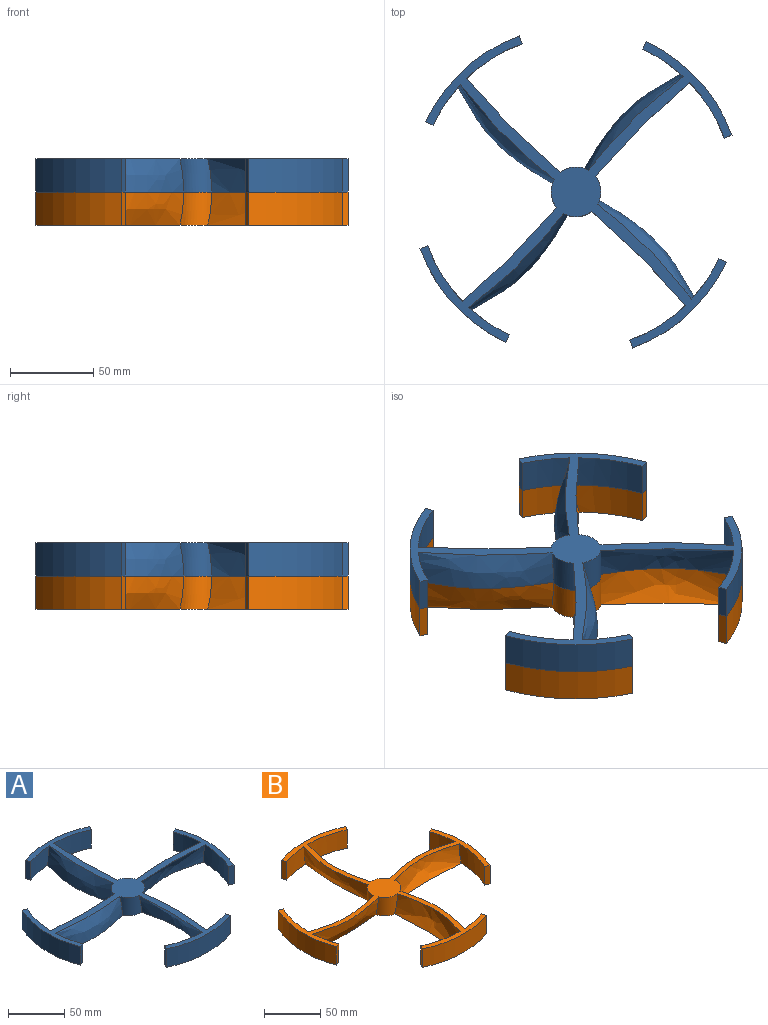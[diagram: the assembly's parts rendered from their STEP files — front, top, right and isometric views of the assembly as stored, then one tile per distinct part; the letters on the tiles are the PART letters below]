
ASSEMBLY  parts=2 mates=1
PART A: 34 faces, bbox 200.4x200.4x20.4 mm
  f0: cylinder r=15mm len=20mm, axis (0,0,-1), area 366.7mm2, adj f3,f4,f6,f14
  f1: cylinder r=15mm len=20mm, axis (0,0,-1), area 366.7mm2, adj f3,f4,f7,f21
  f2: cylinder r=15mm len=20mm, axis (0,0,-1), area 366.7mm2, adj f3,f4,f13,f23
  f3: plane 200.42x200.42mm, normal (0,0,1), area 4211.3mm2, adj f0,f1,f2,f5,f6,f7,f8,f9
  f4: plane 200.29x200.29mm, normal (0,0,-1), area 3850.5mm2, adj f0,f1,f2,f5,f6,f7,f8,f9
  f5: cylinder r=15mm len=20mm, axis (0,0,-1), area 366.7mm2, adj f3,f4,f20,f22
  f6: bspline ~81.35x20mm, area 1709.6mm2, adj f0,f3,f4,f29
  f7: bspline ~80.1x20mm, area 1727.7mm2, adj f1,f3,f4,f30
  f8: cylinder r=95mm len=28.78mm, axis (0,0,-1), area 568.9mm2, adj f3,f4,f9,f13
  f9: plane 20x4.7mm, normal (-0.34,0.94,0), area 100mm2, adj f3,f4,f8,f10
  f10: cylinder r=100mm len=76.46mm, axis (0,0,-1), area 1570.8mm2, adj f3,f4,f9,f11
  f11: plane 20x4.53mm, normal (-0.42,-0.91,0), area 100mm2, adj f3,f4,f10,f12
  f12: cylinder r=95mm len=40.82mm, axis (0,0,-1), area 818.3mm2, adj f3,f4,f11,f14
  f13: bspline ~81.35x20mm, area 1709.6mm2, adj f2,f3,f4,f8
  f14: bspline ~80.1x20mm, area 1727.7mm2, adj f0,f3,f4,f12
  f15: cylinder r=95mm len=28.78mm, axis (0,0,-1), area 568.9mm2, adj f3,f4,f16,f21
  f16: plane 20x4.7mm, normal (0.34,-0.94,0), area 100mm2, adj f3,f4,f15,f17
  f17: cylinder r=100mm len=76.46mm, axis (0,0,-1), area 1570.8mm2, adj f3,f4,f16,f18
  f18: plane 20x4.53mm, normal (0.42,0.91,0), area 100mm2, adj f3,f4,f17,f19
  f19: cylinder r=95mm len=40.82mm, axis (0,0,-1), area 818.3mm2, adj f3,f4,f18,f20
  f20: bspline ~80.1x20mm, area 1727.7mm2, adj f3,f4,f5,f19
  f21: bspline ~81.35x20mm, area 1709.6mm2, adj f1,f3,f4,f15
  f22: bspline ~81.35x20mm, area 1709.6mm2, adj f3,f4,f5,f24
  f23: bspline ~80.1x20mm, area 1727.7mm2, adj f2,f3,f4,f28
  f24: cylinder r=95mm len=28.78mm, axis (0,0,-1), area 568.9mm2, adj f3,f4,f22,f27
  f25: plane 20x4.53mm, normal (0.91,-0.42,0), area 100mm2, adj f3,f4,f26,f28
  f26: cylinder r=100mm len=76.46mm, axis (0,0,-1), area 1570.8mm2, adj f3,f4,f25,f27
  f27: plane 20x4.7mm, normal (-0.94,-0.34,0), area 100mm2, adj f3,f4,f24,f26
  f28: cylinder r=95mm len=40.82mm, axis (0,0,-1), area 818.3mm2, adj f3,f4,f23,f25
  f29: cylinder r=95mm len=28.78mm, axis (0,0,-1), area 568.9mm2, adj f3,f4,f6,f33
  f30: cylinder r=95mm len=40.82mm, axis (0,0,-1), area 818.3mm2, adj f3,f4,f7,f31
  f31: plane 20x4.53mm, normal (-0.91,0.42,0), area 100mm2, adj f3,f4,f30,f32
  f32: cylinder r=100mm len=76.46mm, axis (0,0,-1), area 1570.8mm2, adj f3,f4,f31,f33
  f33: plane 20x4.7mm, normal (0.94,0.34,0), area 100mm2, adj f3,f4,f29,f32
PART B: 34 faces, bbox 200.4x200.4x20.4 mm
  f0: cylinder r=15mm len=20mm, axis (0,0,-1), area 366.7mm2, adj f24,f25,f28,f33
  f1: cylinder r=15mm len=20mm, axis (0,0,-1), area 366.7mm2, adj f24,f26,f30,f33
  f2: cylinder r=15mm len=20mm, axis (0,0,-1), area 366.7mm2, adj f24,f27,f32,f33
  f3: cylinder r=15mm len=20mm, axis (0,0,-1), area 366.7mm2, adj f24,f29,f31,f33
  f4: cylinder r=95mm len=28.78mm, axis (0,0,-1), area 568.9mm2, adj f5,f24,f27,f33
  f5: plane 20x4.7mm, normal (-0.34,0.94,0), area 100mm2, adj f4,f6,f24,f33
  f6: cylinder r=100mm len=76.46mm, axis (0,0,-1), area 1570.8mm2, adj f5,f7,f24,f33
  f7: plane 20x4.53mm, normal (-0.42,-0.91,0), area 100mm2, adj f6,f8,f24,f33
  f8: cylinder r=95mm len=40.82mm, axis (0,0,-1), area 818.3mm2, adj f7,f24,f28,f33
  f9: cylinder r=95mm len=28.78mm, axis (0,0,-1), area 568.9mm2, adj f10,f24,f30,f33
  f10: plane 20x4.7mm, normal (0.34,-0.94,0), area 100mm2, adj f9,f11,f24,f33
  f11: cylinder r=100mm len=76.46mm, axis (0,0,-1), area 1570.8mm2, adj f10,f12,f24,f33
  f12: plane 20x4.53mm, normal (0.42,0.91,0), area 100mm2, adj f11,f13,f24,f33
  f13: cylinder r=95mm len=40.82mm, axis (0,0,-1), area 818.3mm2, adj f12,f24,f29,f33
  f14: cylinder r=95mm len=28.78mm, axis (0,0,-1), area 568.9mm2, adj f17,f24,f31,f33
  f15: plane 20x4.53mm, normal (0.91,-0.42,0), area 100mm2, adj f16,f18,f24,f33
  f16: cylinder r=100mm len=76.46mm, axis (0,0,-1), area 1570.8mm2, adj f15,f17,f24,f33
  f17: plane 20x4.7mm, normal (-0.94,-0.34,0), area 100mm2, adj f14,f16,f24,f33
  f18: cylinder r=95mm len=40.82mm, axis (0,0,-1), area 818.3mm2, adj f15,f24,f32,f33
  f19: cylinder r=95mm len=28.78mm, axis (0,0,-1), area 568.9mm2, adj f23,f24,f25,f33
  f20: cylinder r=95mm len=40.82mm, axis (0,0,-1), area 818.3mm2, adj f21,f24,f26,f33
  f21: plane 20x4.53mm, normal (-0.91,0.42,0), area 100mm2, adj f20,f22,f24,f33
  f22: cylinder r=100mm len=76.46mm, axis (0,0,-1), area 1570.8mm2, adj f21,f23,f24,f33
  f23: plane 20x4.7mm, normal (0.94,0.34,0), area 100mm2, adj f19,f22,f24,f33
  f24: plane 200.42x200.42mm, normal (0,0,-1), area 4211.3mm2, adj f0,f1,f2,f3,f4,f5,f6,f7
  f25: bspline ~81.35x20mm, area 1709.6mm2, adj f0,f19,f24,f33
  f26: bspline ~80.1x20mm, area 1727.7mm2, adj f1,f20,f24,f33
  f27: bspline ~81.35x20mm, area 1709.6mm2, adj f2,f4,f24,f33
  f28: bspline ~80.1x20mm, area 1727.7mm2, adj f0,f8,f24,f33
  f29: bspline ~80.1x20mm, area 1727.7mm2, adj f3,f13,f24,f33
  f30: bspline ~81.35x20mm, area 1709.6mm2, adj f1,f9,f24,f33
  f31: bspline ~81.35x20mm, area 1709.6mm2, adj f3,f14,f24,f33
  f32: bspline ~80.1x20mm, area 1727.7mm2, adj f2,f18,f24,f33
  f33: plane 200.3x200.3mm, normal (0,0,1), area 3845.6mm2, adj f0,f1,f2,f3,f4,f5,f6,f7
PLACE A rot(axis=(0,0,-1),45deg) t=(53.55,124.51,-13.72)mm
PLACE B rot(axis=(0,0,-1),45deg) t=(53.55,124.51,-13.72)mm
MATE fastened A.f9 <-> B.f5  axis (0.42,0.91,0) through (141.91,83.3,-13.72)mm
